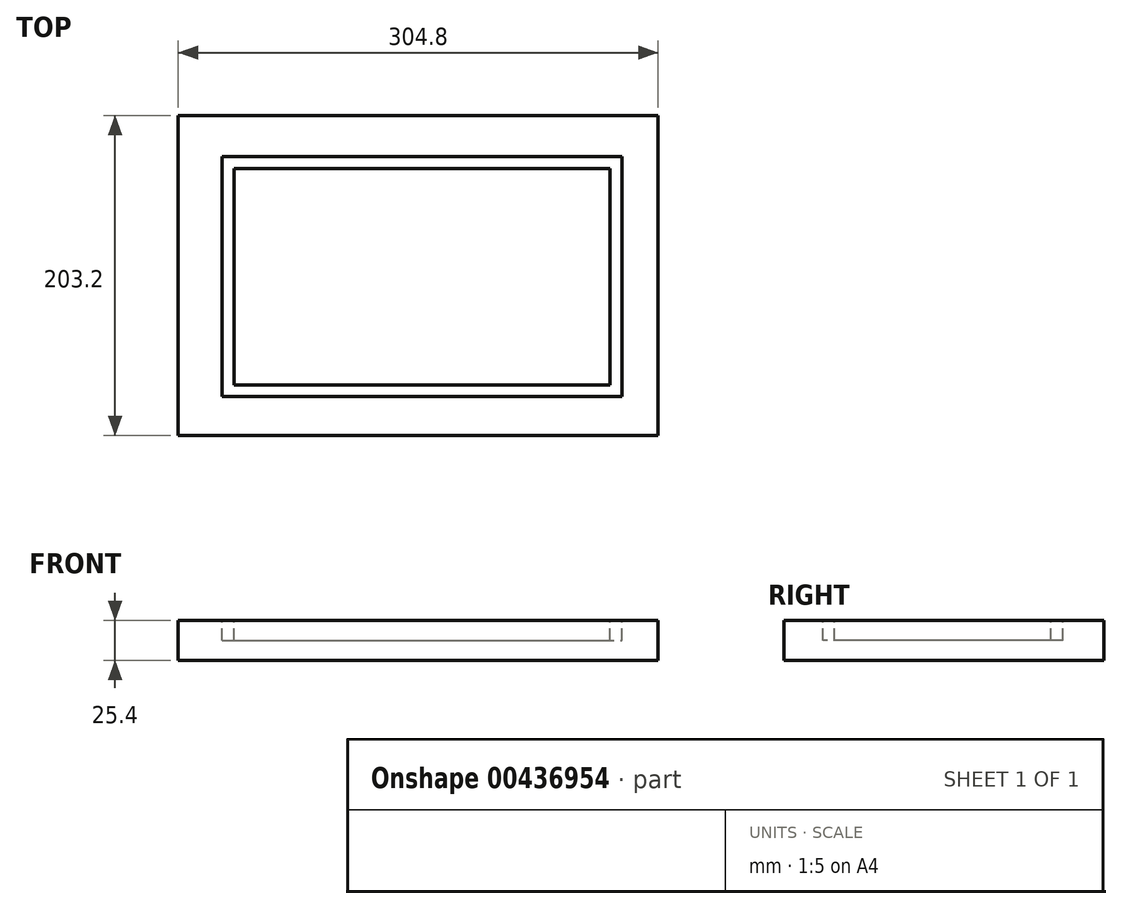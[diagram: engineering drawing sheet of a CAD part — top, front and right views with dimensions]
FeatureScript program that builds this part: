
annotation { "Feature Type Name" : "Feature", "Feature Type Description" : "" }
export const myFeature = defineFeature(function(context is Context, id is Id, definition is map)
    precondition{}
    {
        {
            var Q0;
            Q0=qCreatedBy(makeId("Top.planeOp"),FACE);
            var sketch = newSketch(context, id + "F0", { "sketchPlane" : qUnion([Q0])});
            skLineSegment(sketch, "E0.bottom", {"start": v(0, 0) * mm, "end": v(304.8, 0) * mm});
            skLineSegment(sketch, "E0.top", {"start": v(0, 203.2) * mm, "end": v(304.8, 203.2) * mm});
            skLineSegment(sketch, "E0.left", {"start": v(0, 0) * mm, "end": v(0, 203.2) * mm});
            skLineSegment(sketch, "E0.right", {"start": v(304.8, 0) * mm, "end": v(304.8, 203.2) * mm});
            skSolve(sketch);
        }
        {
            var Q0;
            Q0=makeQuery(id+"F0.imprint","IMPRINT",FACE,{"disambiguationData":[TD([[makeQuery(id+"F0.imprint","IMPRINT",EDGE,{"derivedFrom":sQuery(id+"F0.wireOp",EDGE,"E0.bottom")}),1.0]])]});
            extrude(context, id + "F1", {"entities" : qUnion([Q0]), "depth" : 25.4 * mm});
        }
        {
            var Q0;
            Q0=makeQuery(id+"F1.opExtrude","CAP_FACE",FACE,{"disambiguationData":[OSD([sQuery(id+"F0.wireOp",EDGE,"E0.bottom"),sQuery(id+"F0.wireOp",EDGE,"E0.top"),sQuery(id+"F0.wireOp",EDGE,"E0.left"),sQuery(id+"F0.wireOp",EDGE,"E0.right")])],"isStart":false});
            var sketch = newSketch(context, id + "F2", { "sketchPlane" : qUnion([Q0])});
            skLineSegment(sketch, "E1.bottom", {"start": v(27.84, 176.98) * mm, "end": v(281.84, 176.98) * mm});
            skLineSegment(sketch, "E1.top", {"start": v(27.84, 24.58) * mm, "end": v(281.84, 24.58) * mm});
            skLineSegment(sketch, "E1.left", {"start": v(27.84, 176.98) * mm, "end": v(27.84, 24.58) * mm});
            skLineSegment(sketch, "E1.right", {"start": v(281.84, 176.98) * mm, "end": v(281.84, 24.58) * mm});
            skLineSegment(sketch, "E2.bottom", {"start": v(35.34, 169.48) * mm, "end": v(274.34, 169.48) * mm});
            skLineSegment(sketch, "E2.top", {"start": v(35.34, 32.08) * mm, "end": v(274.34, 32.08) * mm});
            skLineSegment(sketch, "E2.left", {"start": v(35.34, 169.48) * mm, "end": v(35.34, 32.08) * mm});
            skLineSegment(sketch, "E2.right", {"start": v(274.34, 169.48) * mm, "end": v(274.34, 32.08) * mm});
            skSolve(sketch);
        }
        {
            var Q0;
            Q0 = qSketchRegion(id + "F2", true);
            extrude(context, id + "F3", {"entities" : qUnion([Q0]), "operationType" : NewBodyOperationType.REMOVE, "oppositeDirection" : true, "depth" : 12.7 * mm});
        }
    });
